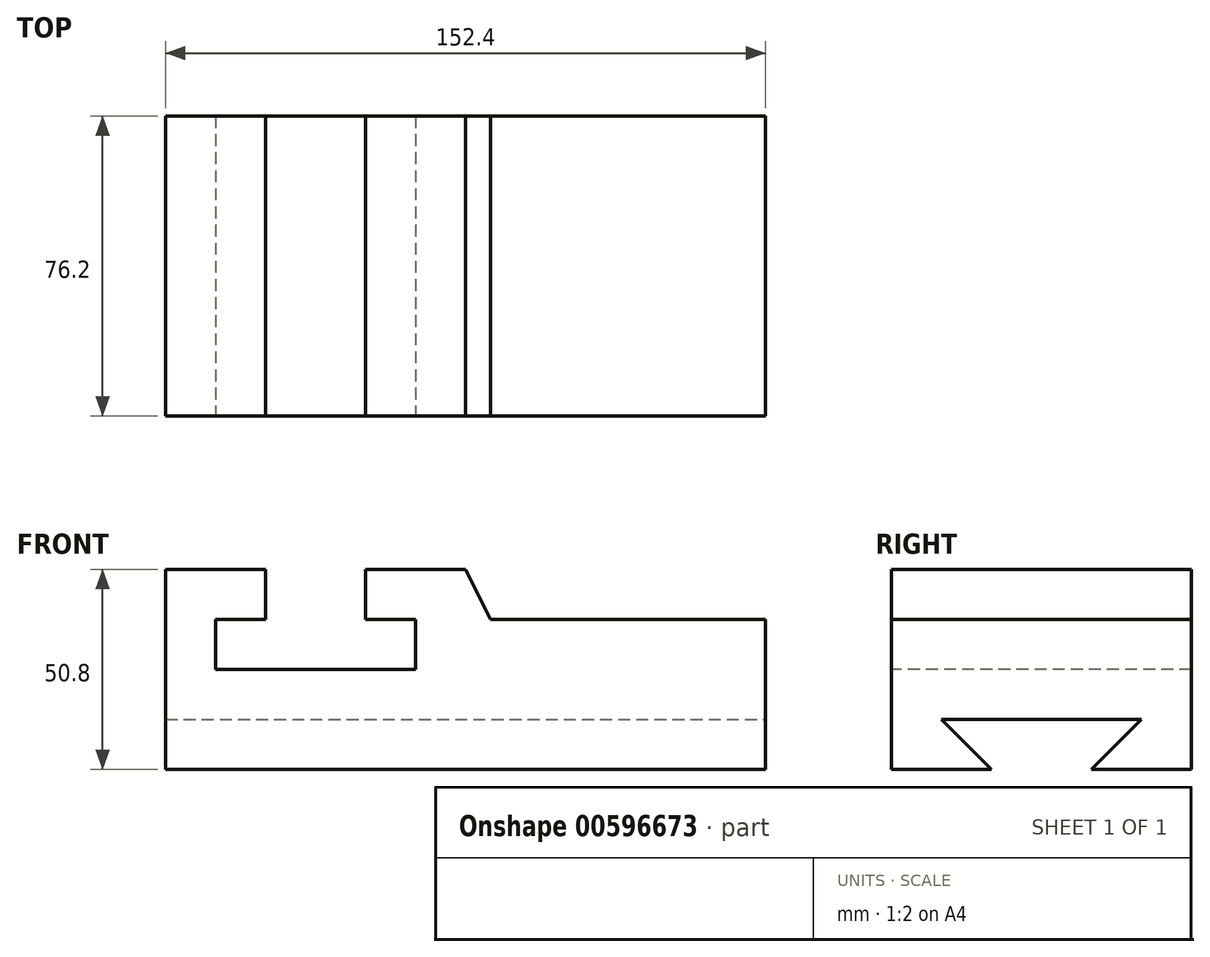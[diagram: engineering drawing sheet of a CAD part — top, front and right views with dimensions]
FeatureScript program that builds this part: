
annotation { "Feature Type Name" : "Feature", "Feature Type Description" : "" }
export const myFeature = defineFeature(function(context is Context, id is Id, definition is map)
    precondition{}
    {
        {
            var Q0;
            Q0=qCreatedBy(makeId("Top.planeOp"),FACE);
            var sketch = newSketch(context, id + "F0", { "sketchPlane" : qUnion([Q0])});
            skLineSegment(sketch, "E0", {"start": v(0, 0) * mm, "end": v(0, 76.2) * mm});
            skLineSegment(sketch, "E1", {"start": v(0, 76.2) * mm, "end": v(152.4, 76.2) * mm});
            skLineSegment(sketch, "E2", {"start": v(152.4, 76.2) * mm, "end": v(152.4, 0) * mm});
            skLineSegment(sketch, "E3", {"start": v(152.4, 0) * mm, "end": v(0, 0) * mm});
            skSolve(sketch);
        }
        {
            var Q0;
            Q0=makeQuery(id+"F0.imprint","IMPRINT",FACE,{"disambiguationData":[TD([[makeQuery(id+"F0.imprint","IMPRINT",EDGE,{"derivedFrom":sQuery(id+"F0.wireOp",EDGE,"E0")}),-1.0]])]});
            extrude(context, id + "F1", {"entities" : qUnion([Q0]), "depth" : 50.8 * mm, "offsetDistance" : 25.4 * mm});
        }
        {
            var Q0;
            Q0=makeQuery(id+"F1.opExtrude","SWEPT_FACE",FACE,{"disambiguationData":[OSD([sQuery(id+"F0.wireOp",EDGE,"E3")])]});
            var sketch = newSketch(context, id + "F2", { "sketchPlane" : qUnion([Q0])});
            skLineSegment(sketch, "E4", {"start": v(0, 50.8) * mm, "end": v(25.4, 50.8) * mm});
            skLineSegment(sketch, "E5", {"start": v(25.4, 50.8) * mm, "end": v(25.4, 38.1) * mm});
            skLineSegment(sketch, "E6", {"start": v(25.4, 38.1) * mm, "end": v(12.7, 38.1) * mm});
            skLineSegment(sketch, "E7", {"start": v(12.7, 38.1) * mm, "end": v(12.7, 25.4) * mm});
            skLineSegment(sketch, "E8", {"start": v(12.7, 25.4) * mm, "end": v(63.5, 25.4) * mm});
            skLineSegment(sketch, "E9", {"start": v(63.5, 25.4) * mm, "end": v(63.5, 38.1) * mm});
            skLineSegment(sketch, "E10", {"start": v(63.5, 38.1) * mm, "end": v(50.8, 38.1) * mm});
            skLineSegment(sketch, "E11", {"start": v(50.8, 38.1) * mm, "end": v(50.8, 50.8) * mm});
            skLineSegment(sketch, "E12", {"start": v(50.8, 50.8) * mm, "end": v(25.4, 50.8) * mm});
            skSolve(sketch);
        }
        {
            var Q0;
            Q0=makeQuery(id+"F2.imprint","IMPRINT",FACE,{"disambiguationData":[TD([[makeQuery(id+"F2.imprint","IMPRINT",EDGE,{"derivedFrom":sQuery(id+"F2.wireOp",EDGE,"E5")}),1.0]])]});
            extrude(context, id + "F3", {"entities" : qUnion([Q0]), "operationType" : NewBodyOperationType.REMOVE, "oppositeDirection" : true, "depth" : 76.2 * mm, "offsetDistance" : 25.4 * mm});
        }
        {
            var Q0;
            {var subQ0=sQuery(id+"F0.wireOp",EDGE,"E1");var subQ1=sQuery(id+"F0.wireOp",EDGE,"E2");var subQ2=sQuery(id+"F0.wireOp",EDGE,"E3");Q0=makeQuery(id+"F3.boolean.opBoolean","SPLIT",FACE,{"disambiguationData":[TD([makeQuery(id+"F1.opExtrude","SWEPT_FACE",FACE,{"disambiguationData":[OSD([subQ1])]})])],"derivedFrom":makeQuery(id+"F1.opExtrude","CAP_FACE",FACE,{"disambiguationData":[OSD([sQuery(id+"F0.wireOp",EDGE,"E0"),subQ0,subQ1,subQ2])],"isStart":false})});}
            var sketch = newSketch(context, id + "F4", { "sketchPlane" : qUnion([Q0])});
            skLineSegment(sketch, "E13", {"start": v(152.4, 0) * mm, "end": v(82.55, 0) * mm});
            skLineSegment(sketch, "E14", {"start": v(82.55, 0) * mm, "end": v(82.55, 76.2) * mm});
            skLineSegment(sketch, "E15", {"start": v(82.55, 76.2) * mm, "end": v(152.4, 76.2) * mm});
            skLineSegment(sketch, "E16", {"start": v(152.4, 76.2) * mm, "end": v(152.4, 0) * mm});
            skSolve(sketch);
        }
        {
            var Q0;
            Q0=makeQuery(id+"F4.imprint","IMPRINT",FACE,{"disambiguationData":[TD([[makeQuery(id+"F4.imprint","IMPRINT",EDGE,{"derivedFrom":sQuery(id+"F4.wireOp",EDGE,"E13")}),-1.0]])]});
            extrude(context, id + "F5", {"entities" : qUnion([Q0]), "operationType" : NewBodyOperationType.REMOVE, "oppositeDirection" : true, "depth" : 12.7 * mm, "offsetDistance" : 25.4 * mm});
        }
        {
            var Q0;
            Q0=makeQuery(id+"F1.opExtrude","SWEPT_FACE",FACE,{"disambiguationData":[OSD([sQuery(id+"F0.wireOp",EDGE,"E3")])]});
            var sketch = newSketch(context, id + "F6", { "sketchPlane" : qUnion([Q0])});
            skLineSegment(sketch, "E17", {"start": v(82.55, 50.8) * mm, "end": v(76.2, 50.8) * mm});
            skLineSegment(sketch, "E18", {"start": v(76.2, 50.8) * mm, "end": v(82.55, 38.1) * mm});
            skSolve(sketch);
        }
        {
            var Q0;
            Q0=makeQuery(id+"F6.imprint","IMPRINT",FACE,{"disambiguationData":[TD([[makeQuery(id+"F6.imprint","IMPRINT",EDGE,{"derivedFrom":sQuery(id+"F6.wireOp",EDGE,"E17")}),1.0]])]});
            extrude(context, id + "F7", {"entities" : qUnion([Q0]), "operationType" : NewBodyOperationType.REMOVE, "oppositeDirection" : true, "depth" : 76.2 * mm, "offsetDistance" : 25.4 * mm});
        }
        {
            var Q0;
            Q0=makeQuery(id+"F1.opExtrude","SWEPT_FACE",FACE,{"disambiguationData":[OSD([sQuery(id+"F0.wireOp",EDGE,"E2")])]});
            var sketch = newSketch(context, id + "F8", { "sketchPlane" : qUnion([Q0])});
            skLineSegment(sketch, "E19", {"start": v(25.4, 0) * mm, "end": v(50.8, 0) * mm});
            skLineSegment(sketch, "E20", {"start": v(50.8, 0) * mm, "end": v(50.8, 12.7) * mm});
            skLineSegment(sketch, "E21", {"start": v(50.8, 12.7) * mm, "end": v(25.4, 12.7) * mm});
            skLineSegment(sketch, "E22", {"start": v(25.4, 12.7) * mm, "end": v(25.4, 0) * mm});
            skSolve(sketch);
        }
        {
            var Q0;
            Q0=makeQuery(id+"F8.imprint","IMPRINT",FACE,{"disambiguationData":[TD([[makeQuery(id+"F8.imprint","IMPRINT",EDGE,{"derivedFrom":sQuery(id+"F8.wireOp",EDGE,"E19")}),-1.0]])]});
            extrude(context, id + "F9", {"entities" : qUnion([Q0]), "operationType" : NewBodyOperationType.REMOVE, "oppositeDirection" : true, "depth" : 152.4 * mm, "offsetDistance" : 25.4 * mm});
        }
        {
            var Q0;
            Q0=makeQuery(id+"F1.opExtrude","SWEPT_FACE",FACE,{"disambiguationData":[OSD([sQuery(id+"F0.wireOp",EDGE,"E2")])]});
            var sketch = newSketch(context, id + "F10", { "sketchPlane" : qUnion([Q0])});
            skLineSegment(sketch, "E23", {"start": v(25.4, 12.7) * mm, "end": v(12.7, 12.7) * mm});
            skLineSegment(sketch, "E24", {"start": v(12.7, 12.7) * mm, "end": v(25.4, 0) * mm});
            skLineSegment(sketch, "E25", {"start": v(25.4, 0) * mm, "end": v(25.4, 12.7) * mm});
            skSolve(sketch);
        }
        {
            var Q0;
            Q0=makeQuery(id+"F10.imprint","IMPRINT",FACE,{"disambiguationData":[TD([[makeQuery(id+"F10.imprint","IMPRINT",EDGE,{"derivedFrom":sQuery(id+"F10.wireOp",EDGE,"E23")}),1.0]])]});
            extrude(context, id + "F11", {"entities" : qUnion([Q0]), "operationType" : NewBodyOperationType.REMOVE, "oppositeDirection" : true, "depth" : 152.4 * mm, "offsetDistance" : 25.4 * mm});
        }
        {
            var Q0;
            Q0=makeQuery(id+"F1.opExtrude","SWEPT_FACE",FACE,{"disambiguationData":[OSD([sQuery(id+"F0.wireOp",EDGE,"E2")])]});
            var sketch = newSketch(context, id + "F12", { "sketchPlane" : qUnion([Q0])});
            skLineSegment(sketch, "E26", {"start": v(50.8, 12.7) * mm, "end": v(63.5, 12.7) * mm});
            skLineSegment(sketch, "E27", {"start": v(63.5, 12.7) * mm, "end": v(50.8, 0) * mm});
            skLineSegment(sketch, "E28", {"start": v(50.8, 0) * mm, "end": v(50.8, 12.7) * mm});
            skSolve(sketch);
        }
        {
            var Q0;
            Q0=makeQuery(id+"F12.imprint","IMPRINT",FACE,{"disambiguationData":[TD([[makeQuery(id+"F12.imprint","IMPRINT",EDGE,{"derivedFrom":sQuery(id+"F12.wireOp",EDGE,"E26")}),-1.0]])]});
            extrude(context, id + "F13", {"entities" : qUnion([Q0]), "operationType" : NewBodyOperationType.REMOVE, "oppositeDirection" : true, "depth" : 152.4 * mm, "offsetDistance" : 25.4 * mm});
        }
    });
